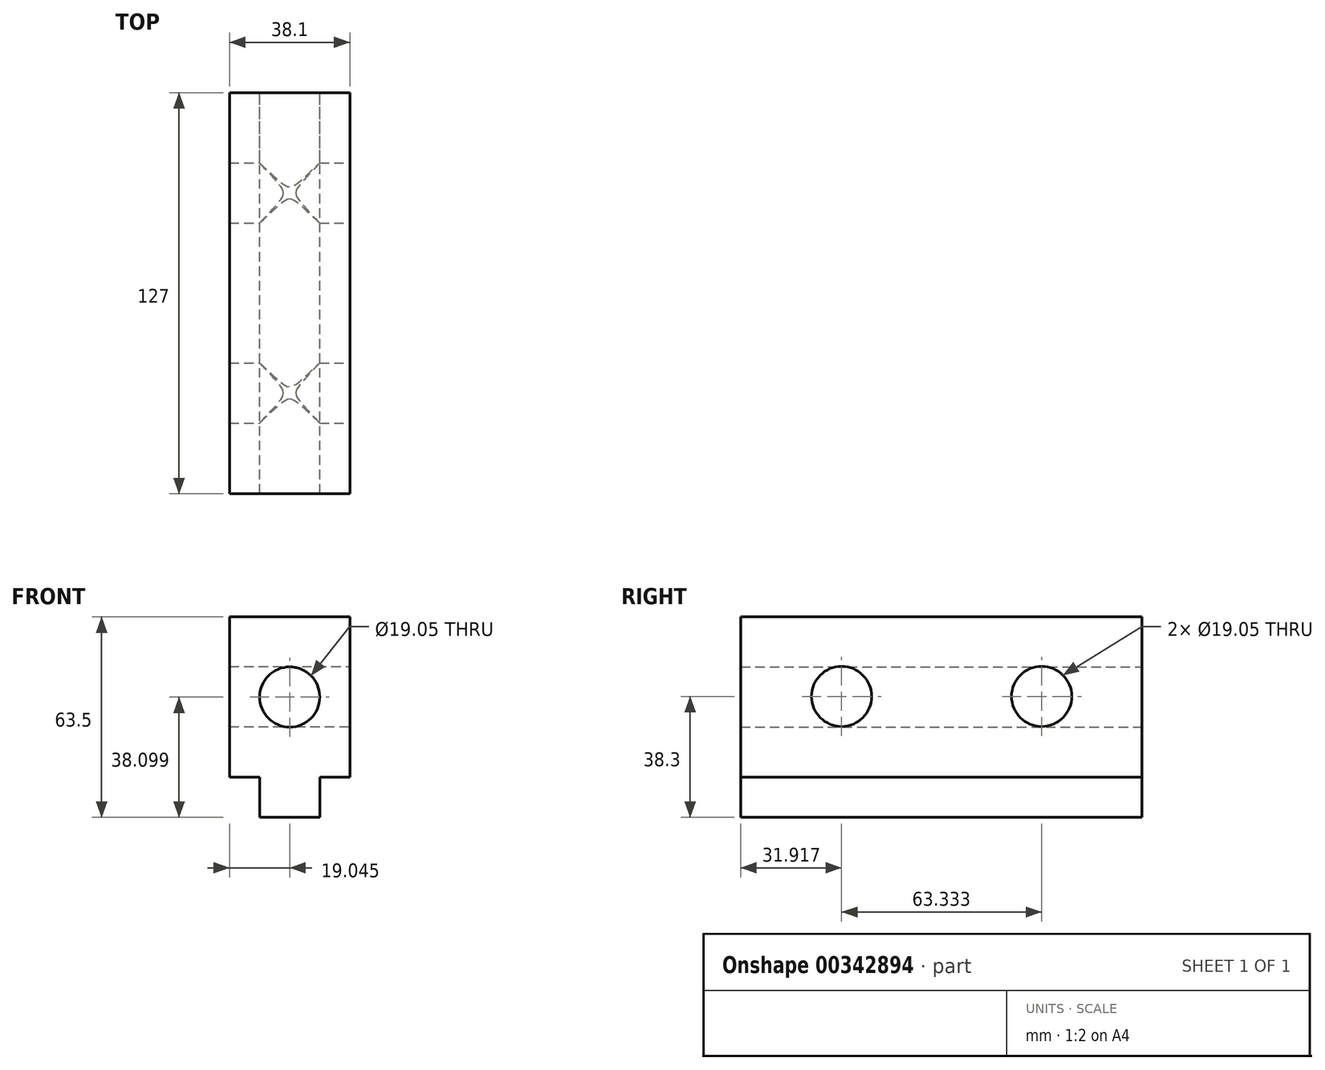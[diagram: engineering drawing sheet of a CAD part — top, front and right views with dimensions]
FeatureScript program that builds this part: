
annotation { "Feature Type Name" : "Feature", "Feature Type Description" : "" }
export const myFeature = defineFeature(function(context is Context, id is Id, definition is map)
    precondition{}
    {
        {
            var Q0;
            Q0=qCreatedBy(makeId("Front.planeOp"),FACE);
            var sketch = newSketch(context, id + "F0", { "sketchPlane" : qUnion([Q0])});
            skLineSegment(sketch, "E0", {"start": v(-52.21, 40.94) * mm, "end": v(-52.21, -9.86) * mm});
            skLineSegment(sketch, "E1", {"start": v(-52.21, -9.86) * mm, "end": v(-42.69, -9.86) * mm});
            skLineSegment(sketch, "E2", {"start": v(-42.69, -9.86) * mm, "end": v(-42.69, -22.56) * mm});
            skLineSegment(sketch, "E3", {"start": v(-42.69, -22.56) * mm, "end": v(-23.64, -22.56) * mm});
            skLineSegment(sketch, "E4", {"start": v(-23.64, -22.56) * mm, "end": v(-23.64, -9.86) * mm});
            skLineSegment(sketch, "E5", {"start": v(-23.64, -9.86) * mm, "end": v(-14.11, -9.86) * mm});
            skLineSegment(sketch, "E6", {"start": v(-14.11, -9.86) * mm, "end": v(-14.11, 40.94) * mm});
            skLineSegment(sketch, "E7", {"start": v(-14.11, 40.94) * mm, "end": v(-52.21, 40.94) * mm});
            skLineSegment(sketch, "E8", {"start": v(-52.21, 40.94) * mm, "end": v(-52.21, 15.54) * mm});
            skCircle(sketch, "E9", {"center": v(-33.16, 15.54) * mm, "radius": 9.53 * mm});
            skPoint(sketch, "E9.centerSnap0", {"position": v(-33.16, 40.94) * mm});
            skSolve(sketch);
        }
        {
            var Q0;
            Q0=makeQuery(id+"F0.imprint","IMPRINT",FACE,{"disambiguationData":[TD([[makeQuery(id+"F0.imprint","IMPRINT",EDGE,{"derivedFrom":sQuery(id+"F0.wireOp",EDGE,"E0")}),1.0]])]});
            extrude(context, id + "F1", {"entities" : qUnion([Q0]), "depth" : 127 * mm});
        }
        {
            var Q0;
            Q0=qCreatedBy(makeId("Right.planeOp"),FACE);
            var sketch = newSketch(context, id + "F2", { "sketchPlane" : qUnion([Q0])});
            skLineSegment(sketch, "E10", {"start": v(0, 43.25) * mm, "end": v(-31.75, 43.25) * mm});
            skLineSegment(sketch, "E11", {"start": v(-126.83, 41.54) * mm, "end": v(-95.08, 41.54) * mm});
            skLineSegment(sketch, "E12", {"start": v(0, 40.95) * mm, "end": v(0, -9.47) * mm});
            skCircle(sketch, "E13", {"center": v(-31.75, 15.74) * mm, "radius": 9.53 * mm});
            skPoint(sketch, "E13.centerSnap0", {"position": v(0, 15.74) * mm});
            skCircle(sketch, "E14", {"center": v(-95.08, 15.74) * mm, "radius": 9.53 * mm});
            skSolve(sketch);
        }
        {
            var Q0;
            Q0=makeQuery(id+"F2.imprint","IMPRINT",FACE,{"disambiguationData":[TD([[makeQuery(id+"F2.imprint","IMPRINT",EDGE,{"derivedFrom":sQuery(id+"F2.wireOp",EDGE,"E14")}),1.0]])]});
            extrude(context, id + "F3", {"entities" : qUnion([Q0]), "operationType" : NewBodyOperationType.REMOVE, "oppositeDirection" : true, "depth" : 129.8 * mm});
        }
        {
            var Q0;
            Q0=makeQuery(id+"F2.imprint","IMPRINT",FACE,{"disambiguationData":[TD([[makeQuery(id+"F2.imprint","IMPRINT",EDGE,{"derivedFrom":sQuery(id+"F2.wireOp",EDGE,"E13")}),1.0]])]});
            extrude(context, id + "F4", {"entities" : qUnion([Q0]), "operationType" : NewBodyOperationType.REMOVE, "oppositeDirection" : true, "depth" : 104.14 * mm});
        }
    });
